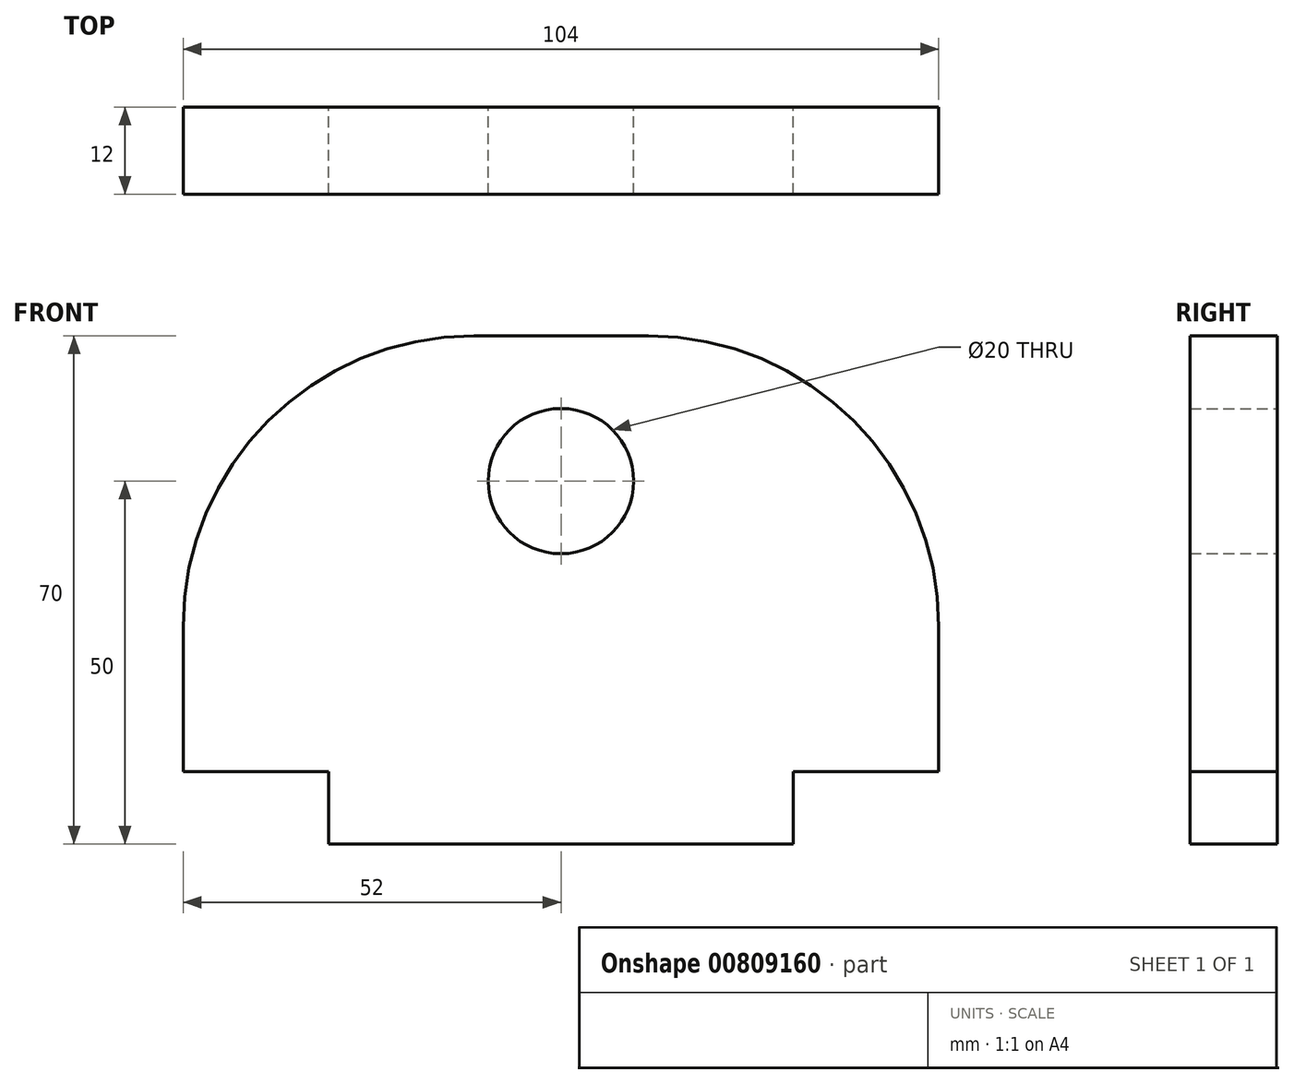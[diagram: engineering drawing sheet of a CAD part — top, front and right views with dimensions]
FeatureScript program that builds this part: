
annotation { "Feature Type Name" : "Feature", "Feature Type Description" : "" }
export const myFeature = defineFeature(function(context is Context, id is Id, definition is map)
    precondition{}
    {
        {
            var Q0;
            Q0=qCreatedBy(makeId("Front.planeOp"),FACE);
            var sketch = newSketch(context, id + "F0", { "sketchPlane" : qUnion([Q0])});
            skLineSegment(sketch, "E0", {"start": v(0, 0) * mm, "end": v(20, 0) * mm});
            skLineSegment(sketch, "E1", {"start": v(20, 0) * mm, "end": v(20, -10) * mm});
            skLineSegment(sketch, "E2", {"start": v(20, -10) * mm, "end": v(84, -10) * mm});
            skLineSegment(sketch, "E3", {"start": v(84, -10) * mm, "end": v(84, 0) * mm});
            skLineSegment(sketch, "E4", {"start": v(84, 0) * mm, "end": v(104, 0) * mm});
            skLineSegment(sketch, "E5", {"start": v(104, 0) * mm, "end": v(104, 20) * mm});
            skLineSegment(sketch, "E6", {"start": v(64, 60) * mm, "end": v(40, 60) * mm});
            skLineSegment(sketch, "E7", {"start": v(0, 20) * mm, "end": v(0, 0) * mm});
            skCircle(sketch, "E8", {"center": v(52, 40) * mm, "radius": 10 * mm});
            skPoint(sketch, "E9.visualSharp", {"position": v(0, 60) * mm});
            skArc(sketch, "E9.filletArc", {"start": v(40, 60) * mm, "mid": v(11.72, 48.28) * mm, "end": v(0, 20) * mm});
            skPoint(sketch, "E10.visualSharp", {"position": v(104, 60) * mm});
            skArc(sketch, "E10.filletArc", {"start": v(104, 20) * mm, "mid": v(92.28, 48.28) * mm, "end": v(64, 60) * mm});
            skSolve(sketch);
        }
        {
            var Q0;
            Q0=makeQuery(id+"F0.imprint","IMPRINT",FACE,{"disambiguationData":[TD([[makeQuery(id+"F0.imprint","IMPRINT",EDGE,{"derivedFrom":sQuery(id+"F0.wireOp",EDGE,"E0")}),1.0]])]});
            extrude(context, id + "F1", {"entities" : qUnion([Q0]), "depth" : 12 * mm, "offsetDistance" : 25 * mm});
        }
    });
